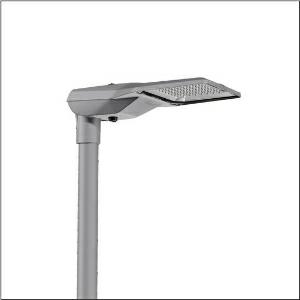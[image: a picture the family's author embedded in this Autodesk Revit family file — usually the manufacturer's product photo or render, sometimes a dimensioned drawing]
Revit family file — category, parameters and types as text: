
# Revit family: streetlight_sl_21_midi___stw1_0a_5xe3e63t08lb_15d1
name_source: partatom
category: Lighting Fixtures
units: mm (PartAtom-declared; Revit-internal decimal feet)

## family parameters
Cut with Voids When Loaded = No
Host = Face
Light Source = No
Part Type = Normal
Room Calculation Point = No
Round Connector Dimension = Use Diameter
Shared = No

## types (1)
- --- (1 x LED, 12860 lm, 99.6 W, 2700K)
    Apparent Load = 100 VA
    CIE Flux Codes = 38 75 98 100 100
    Color Rendering = 70
    Color Temperature = 2700K
    Default Elevation = 1800 mm
    Description = Streetlight SL 21 midi, mast luminaire, primary light control with lens, of PMMA, primary optical cover: cover, of toughened safety glass, transparent, light distribution: STW1.0a, light emission: direct distribution, primary light characteristic: asymmetric, installation type: side-entry, post-top, LED, High Power LED, rated luminous flux: 12.860lm, luminous efficacy: 129lm/W, light colour: 727, colour temperature: 2700K, control gear: D4i, control: overheat protection, constant luminous flux control, time-dependent luminous flux control, flexible luminous flux parameterisation, pre-setting: logarithmic dimming characteristic, mains connection: 230..240V, AC, 50/60Hz, start of lifetime: 100W, end of service life: 102W, reduction: 45W, luminaire housing, of diecast aluminium, powder-coated, SITECO metallic grey (DB 702S), corrosivity category C5 high according to DIN EN ISO 12944, please order mast flange separately, inclination adjustable: 0°, 5°, 10°, 15°, sealing non-destructively replaceable, multi-level sealing system, length: 644mm, width: 335mm, height: 110mm, mast flange for spigot size: 42mm (side-entry): 5XC10008XM4, 60/48mm (side-entry/post-top): 5XC10108XM2, 76/60mm (side-entry/post-top): 5XC10108XM1, mounting height: 4..8m, Smart Interface below and above, protection rating (complete): IP66, insulation class (complete): insulation class II (safety insulation), certification: CE, ENEC, ENEC+, VDE, impact resistance: IK10, permissible operating ambient temperature for outdoor applications: -40..+50°C, standard-compliant lighting for roads and squares, packaging unit: 1 piece

Light Distribution: STW1.0a
    Height = 111 mm
    Lamp = 1 x LED
    Lamp Light Flux = 12860 lm
    Lamp Power = 99.6 W
    Lamp count = 1
    Length = 644 mm
    Luminous efficacy = 129 lm/W
    Manufacturer = Siteco
    ModVariant = No
    Model = 5XE3E63T08LB
    Number of Poles = 1
    OnlyDefault = Yes
    Power Factor = 1
    Product Name = Streetlight SL 21 midi | STW1.0a
    Product group = mast luminaire | pylon top
    ProductGroupID = 6100
    Protection Class = Protection class II
    Protection Degree = IP 66
    RLX_Detail_Level = 1
    RLX_Emergency_Light_Flux = 0 lm
    RLX_Emergency_Type = 0
    RLX_Emergency_Type_DB = No
    RlxData = <blob elided: 26985 chars, md5=61519c88>
    Socket = socket
    Standby Power = 0 W
    System Light Flux = 12860 lm
    System Power = 100 W
    Type Comments = factory setting: luminous flux: 100 % | dim-lin: 254 | 1020 mA
    Type Image = l_1004304.jpg
    URL = http://relux.com
    VarID = @adj_031501
    Voltage = 0 V
    Weight = 0.00 kg
    Width = 336 mm

## geometry (parser evidence)
native form markers: Blend x4, Sweep x12
no freeform markers — native parametric forms only
